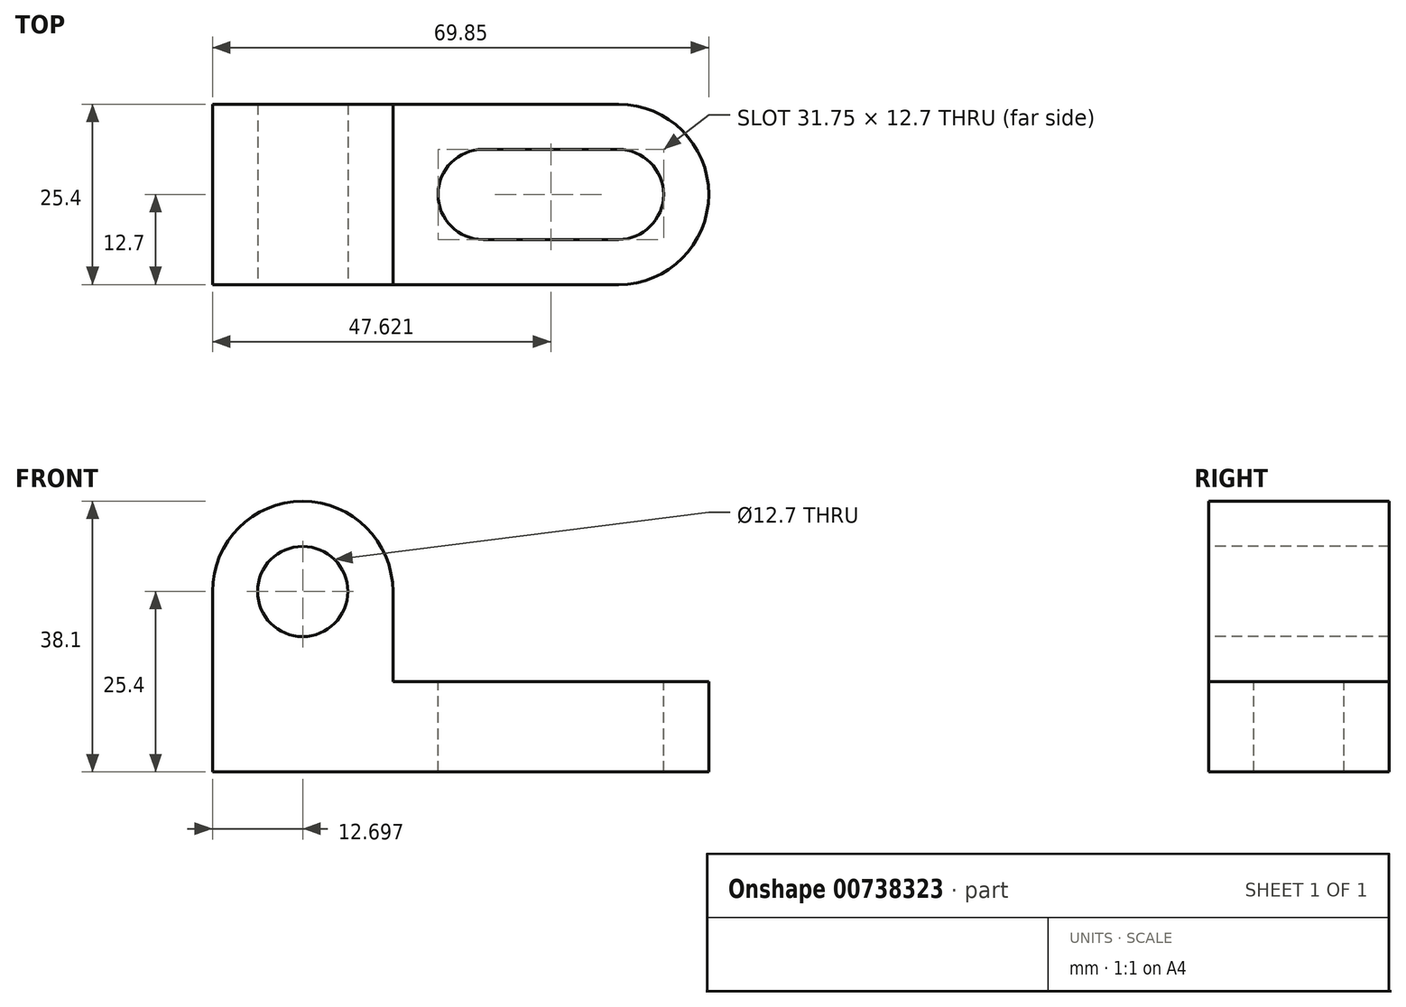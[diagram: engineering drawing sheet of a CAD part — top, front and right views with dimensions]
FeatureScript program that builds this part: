
annotation { "Feature Type Name" : "Feature", "Feature Type Description" : "" }
export const myFeature = defineFeature(function(context is Context, id is Id, definition is map)
    precondition{}
    {
        {
            var Q0;
            Q0=qCreatedBy(makeId("Front.planeOp"),FACE);
            var sketch = newSketch(context, id + "F0", { "sketchPlane" : qUnion([Q0])});
            skLineSegment(sketch, "E0", {"start": v(-50.68, 0) * mm, "end": v(-50.68, 38.1) * mm});
            skLineSegment(sketch, "E1", {"start": v(-50.68, 38.1) * mm, "end": v(-25.28, 38.1) * mm});
            skLineSegment(sketch, "E2", {"start": v(-25.28, 38.1) * mm, "end": v(-25.28, 12.7) * mm});
            skLineSegment(sketch, "E3", {"start": v(-25.28, 12.7) * mm, "end": v(19.17, 12.7) * mm});
            skLineSegment(sketch, "E4", {"start": v(19.17, 12.7) * mm, "end": v(19.17, 0) * mm});
            skLineSegment(sketch, "E5", {"start": v(19.17, 0) * mm, "end": v(-50.68, 0) * mm});
            skLineSegment(sketch, "E6", {"start": v(-50.68, 25.4) * mm, "end": v(-25.28, 25.4) * mm});
            skLineSegment(sketch, "E7", {"start": v(-50.68, 25.4) * mm, "end": v(-50.68, 38.1) * mm});
            skCircle(sketch, "E8", {"center": v(-37.98, 25.4) * mm, "radius": 6.35 * mm});
            skLineSegment(sketch, "E9", {"start": v(-50.68, 25.4) * mm, "end": v(-44.33, 25.4) * mm});
            skArc(sketch, "E10", {"start": v(-25.28, 25.4) * mm, "mid": v(-37.98, 38.1) * mm, "end": v(-50.68, 25.4) * mm});
            skSolve(sketch);
        }
        {
            var Q0;
            {var subQ0=sQuery(id+"F0.wireOp",EDGE,"E1");var subQ1=sQuery(id+"F0.wireOp",EDGE,"E0");var subQ2=makeQuery(id+"F0.imprint","INTERSECT",VERTEX,{"derivedFrom":[subQ1,subQ0]});Q0=makeQuery(id+"F0.imprint","IMPRINT",FACE,{"disambiguationData":[TD([[makeQuery(id+"F0.imprint","IMPRINT",EDGE,{"disambiguationData":[TD([[subQ2,-1.0]])],"derivedFrom":subQ0}),-1.0]])]});}
            var Q1;
            {var subQ1=sQuery(id+"F0.wireOp",EDGE,"E6");var subQ4=sQuery(id+"F0.wireOp",EDGE,"E8");var subQ5=makeQuery(id+"F0.imprint","INTERSECT",VERTEX,{"disambiguationData":[OD(0.0)],"derivedFrom":[subQ1,subQ4]});Q1=makeQuery(id+"F0.imprint","IMPRINT",FACE,{"disambiguationData":[TD([[makeQuery(id+"F0.imprint","IMPRINT",EDGE,{"disambiguationData":[TD([[subQ5,1.0]])],"derivedFrom":subQ4}),-1.0]])]});}
            var Q2;
            {var subQ0=sQuery(id+"F0.wireOp",EDGE,"E2");var subQ1=sQuery(id+"F0.wireOp",EDGE,"E1");var subQ2=makeQuery(id+"F0.imprint","INTERSECT",VERTEX,{"derivedFrom":[subQ1,subQ0]});Q2=makeQuery(id+"F0.imprint","IMPRINT",FACE,{"disambiguationData":[TD([[makeQuery(id+"F0.imprint","IMPRINT",EDGE,{"disambiguationData":[TD([[subQ2,1.0]])],"derivedFrom":subQ1}),-1.0]])]});}
            var Q3;
            {var subQ0=sQuery(id+"F0.wireOp",EDGE,"E8");var subQ1=sQuery(id+"F0.wireOp",EDGE,"E6");var subQ2=makeQuery(id+"F0.imprint","INTERSECT",VERTEX,{"disambiguationData":[OD(0.0)],"derivedFrom":[subQ1,subQ0]});Q3=makeQuery(id+"F0.imprint","IMPRINT",FACE,{"disambiguationData":[TD([[makeQuery(id+"F0.imprint","IMPRINT",EDGE,{"disambiguationData":[TD([[subQ2,-1.0]])],"derivedFrom":subQ1}),1.0]])]});}
            var Q4;
            {var subQ0=sQuery(id+"F0.wireOp",EDGE,"E8");var subQ1=sQuery(id+"F0.wireOp",EDGE,"E6");var subQ2=makeQuery(id+"F0.imprint","INTERSECT",VERTEX,{"disambiguationData":[OD(0.0)],"derivedFrom":[subQ1,subQ0]});Q4=makeQuery(id+"F0.imprint","IMPRINT",FACE,{"disambiguationData":[TD([[makeQuery(id+"F0.imprint","IMPRINT",EDGE,{"disambiguationData":[TD([[subQ2,-1.0]])],"derivedFrom":subQ1}),-1.0]])]});}
            var Q5;
            {var subQ0=sQuery(id+"F0.wireOp",EDGE,"E3");Q5=makeQuery(id+"F0.imprint","IMPRINT",FACE,{"disambiguationData":[TD([[makeQuery(id+"F0.imprint","IMPRINT",EDGE,{"derivedFrom":subQ0}),-1.0]])]});}
            extrude(context, id + "F1", {"entities" : qUnion([Q0, Q1, Q2, Q3, Q4, Q5]), "depth" : 25.4 * mm, "offsetDistance" : 25.4 * mm});
        }
        {
            var Q0;
            Q0=makeQuery(id+"F1.opExtrude","CAP_FACE",FACE,{"disambiguationData":[OSD([sQuery(id+"F0.wireOp",EDGE,"E0"),sQuery(id+"F0.wireOp",EDGE,"E1"),sQuery(id+"F0.wireOp",EDGE,"E2"),sQuery(id+"F0.wireOp",EDGE,"E3"),sQuery(id+"F0.wireOp",EDGE,"E4"),sQuery(id+"F0.wireOp",EDGE,"E5")])],"isStart":false});
            var sketch = newSketch(context, id + "F2", { "sketchPlane" : qUnion([Q0])});
            skLineSegment(sketch, "E11", {"start": v(-50.68, 25.4) * mm, "end": v(-25.28, 25.4) * mm});
            skLineSegment(sketch, "E12", {"start": v(-25.28, 38.1) * mm, "end": v(-25.28, 25.4) * mm});
            skCircle(sketch, "E13", {"center": v(-37.98, 25.4) * mm, "radius": 6.35 * mm});
            skArc(sketch, "E14", {"start": v(-25.28, 25.4) * mm, "mid": v(-37.98, 38.1) * mm, "end": v(-50.68, 25.4) * mm});
            skSolve(sketch);
        }
        {
            var Q0;
            {var subQ1=makeQuery(id+"F1.opExtrude","CAP_EDGE",EDGE,{"disambiguationData":[OSD([sQuery(id+"F0.wireOp",EDGE,"E0")])],"isStart":false});var subQ3=makeQuery(id+"F1.opExtrude","CAP_EDGE",EDGE,{"disambiguationData":[OSD([sQuery(id+"F0.wireOp",EDGE,"E1")])],"isStart":false});var subQ5=makeQuery(id+"F2.imprint","INTERSECT",VERTEX,{"derivedFrom":[subQ1,subQ3]});Q0=makeQuery(id+"F2.imprint","IMPRINT",FACE,{"disambiguationData":[TD([[makeQuery(id+"F2.imprint","IMPRINT",EDGE,{"disambiguationData":[TD([[subQ5,-1.0]])],"derivedFrom":subQ3}),-1.0]])]});}
            var Q1;
            {var subQ0=sQuery(id+"F2.wireOp",EDGE,"E12");Q1=makeQuery(id+"F2.imprint","IMPRINT",FACE,{"disambiguationData":[TD([[makeQuery(id+"F2.imprint","IMPRINT",EDGE,{"derivedFrom":subQ0}),-1.0]])]});}
            var Q2;
            {var subQ0=sQuery(id+"F2.wireOp",EDGE,"E13");var subQ1=sQuery(id+"F2.wireOp",EDGE,"E11");var subQ2=makeQuery(id+"F2.imprint","INTERSECT",VERTEX,{"disambiguationData":[OD(0.0)],"derivedFrom":[subQ1,subQ0]});Q2=makeQuery(id+"F2.imprint","IMPRINT",FACE,{"disambiguationData":[TD([[makeQuery(id+"F2.imprint","IMPRINT",EDGE,{"disambiguationData":[TD([[subQ2,-1.0]])],"derivedFrom":subQ1}),1.0]])]});}
            var Q3;
            {var subQ0=sQuery(id+"F2.wireOp",EDGE,"E13");var subQ1=sQuery(id+"F2.wireOp",EDGE,"E11");var subQ2=makeQuery(id+"F2.imprint","INTERSECT",VERTEX,{"disambiguationData":[OD(0.0)],"derivedFrom":[subQ1,subQ0]});Q3=makeQuery(id+"F2.imprint","IMPRINT",FACE,{"disambiguationData":[TD([[makeQuery(id+"F2.imprint","IMPRINT",EDGE,{"disambiguationData":[TD([[subQ2,-1.0]])],"derivedFrom":subQ1}),-1.0]])]});}
            extrude(context, id + "F3", {"entities" : qUnion([Q0, Q1, Q2, Q3]), "operationType" : NewBodyOperationType.REMOVE, "endBound" : BoundingType.THROUGH_ALL, "oppositeDirection" : true, "depth" : 25.4 * mm, "offsetDistance" : 25.4 * mm});
        }
        {
            var Q0;
            Q0=makeQuery(id+"F1.opExtrude","SWEPT_FACE",FACE,{"disambiguationData":[OSD([sQuery(id+"F0.wireOp",EDGE,"E3")])]});
            var sketch = newSketch(context, id + "F4", { "sketchPlane" : qUnion([Q0])});
            skLineSegment(sketch, "E15", {"start": v(-12.58, 0) * mm, "end": v(-12.58, -25.4) * mm});
            skLineSegment(sketch, "E16", {"start": v(6.47, 0) * mm, "end": v(6.47, -25.4) * mm});
            skLineSegment(sketch, "E17", {"start": v(6.47, 0) * mm, "end": v(19.17, 0) * mm});
            skLineSegment(sketch, "E18", {"start": v(-12.58, 0) * mm, "end": v(-25.28, 0) * mm});
            skCircle(sketch, "E19", {"center": v(-12.58, -12.7) * mm, "radius": 6.35 * mm});
            skCircle(sketch, "E20", {"center": v(6.47, -12.7) * mm, "radius": 6.35 * mm});
            skArc(sketch, "E21", {"start": v(6.47, -25.4) * mm, "mid": v(19.17, -12.7) * mm, "end": v(6.47, 0) * mm});
            skLineSegment(sketch, "E22", {"start": v(-12.58, -6.35) * mm, "end": v(6.47, -6.35) * mm});
            skLineSegment(sketch, "E23", {"start": v(6.47, -19.05) * mm, "end": v(-12.58, -19.05) * mm});
            skSolve(sketch);
        }
        {
            var Q0;
            {var subQ0=sQuery(id+"F4.wireOp",EDGE,"E19");var subQ1=sQuery(id+"F4.wireOp",EDGE,"E15");var subQ2=makeQuery(id+"F4.imprint","INTERSECT",VERTEX,{"derivedFrom":[subQ1,subQ0,sQuery(id+"F4.wireOp",EDGE,"E22")]});Q0=makeQuery(id+"F4.imprint","IMPRINT",FACE,{"disambiguationData":[TD([[makeQuery(id+"F4.imprint","IMPRINT",EDGE,{"disambiguationData":[TD([[subQ2,-1.0]])],"derivedFrom":subQ1}),1.0]])]});}
            var Q1;
            {var subQ0=sQuery(id+"F4.wireOp",EDGE,"E19");var subQ1=sQuery(id+"F4.wireOp",EDGE,"E15");var subQ2=makeQuery(id+"F4.imprint","INTERSECT",VERTEX,{"derivedFrom":[subQ1,subQ0,sQuery(id+"F4.wireOp",EDGE,"E22")]});Q1=makeQuery(id+"F4.imprint","IMPRINT",FACE,{"disambiguationData":[TD([[makeQuery(id+"F4.imprint","IMPRINT",EDGE,{"disambiguationData":[TD([[subQ2,-1.0]])],"derivedFrom":subQ1}),-1.0]])]});}
            var Q2;
            {var subQ0=sQuery(id+"F4.wireOp",EDGE,"E22");Q2=makeQuery(id+"F4.imprint","IMPRINT",FACE,{"disambiguationData":[TD([[makeQuery(id+"F4.imprint","IMPRINT",EDGE,{"derivedFrom":subQ0}),-1.0]])]});}
            var Q3;
            {var subQ0=sQuery(id+"F4.wireOp",EDGE,"E20");var subQ1=sQuery(id+"F4.wireOp",EDGE,"E16");var subQ2=makeQuery(id+"F4.imprint","INTERSECT",VERTEX,{"derivedFrom":[subQ1,subQ0,sQuery(id+"F4.wireOp",EDGE,"E22")]});Q3=makeQuery(id+"F4.imprint","IMPRINT",FACE,{"disambiguationData":[TD([[makeQuery(id+"F4.imprint","IMPRINT",EDGE,{"disambiguationData":[TD([[subQ2,-1.0]])],"derivedFrom":subQ1}),-1.0]])]});}
            var Q4;
            {var subQ0=sQuery(id+"F4.wireOp",EDGE,"E20");var subQ1=sQuery(id+"F4.wireOp",EDGE,"E16");var subQ2=makeQuery(id+"F4.imprint","INTERSECT",VERTEX,{"derivedFrom":[subQ1,subQ0,sQuery(id+"F4.wireOp",EDGE,"E22")]});Q4=makeQuery(id+"F4.imprint","IMPRINT",FACE,{"disambiguationData":[TD([[makeQuery(id+"F4.imprint","IMPRINT",EDGE,{"disambiguationData":[TD([[subQ2,-1.0]])],"derivedFrom":subQ1}),1.0]])]});}
            var Q5;
            {var subQ0=sQuery(id+"F4.wireOp",EDGE,"E17");Q5=makeQuery(id+"F4.imprint","IMPRINT",FACE,{"disambiguationData":[TD([[makeQuery(id+"F4.imprint","IMPRINT",EDGE,{"derivedFrom":subQ0}),-1.0]])]});}
            var Q6;
            {var subQ0=sQuery(id+"F4.wireOp",EDGE,"E21");var subQ1=sQuery(id+"F0.wireOp",EDGE,"E3");var subQ2=makeQuery(id+"F1.opExtrude","CAP_EDGE",EDGE,{"disambiguationData":[OSD([subQ1])],"isStart":false});var subQ3=makeQuery(id+"F4.imprint","INTERSECT",VERTEX,{"derivedFrom":[subQ2,sQuery(id+"F4.wireOp",EDGE,"E16"),subQ0]});Q6=makeQuery(id+"F4.imprint","IMPRINT",FACE,{"disambiguationData":[TD([[makeQuery(id+"F4.imprint","IMPRINT",EDGE,{"disambiguationData":[TD([[subQ3,-1.0]])],"derivedFrom":subQ0}),-1.0]])]});}
            extrude(context, id + "F5", {"entities" : qUnion([Q0, Q1, Q2, Q3, Q4, Q5, Q6]), "operationType" : NewBodyOperationType.REMOVE, "endBound" : BoundingType.THROUGH_ALL, "oppositeDirection" : true, "depth" : 25.4 * mm, "offsetDistance" : 25.4 * mm});
        }
    });
